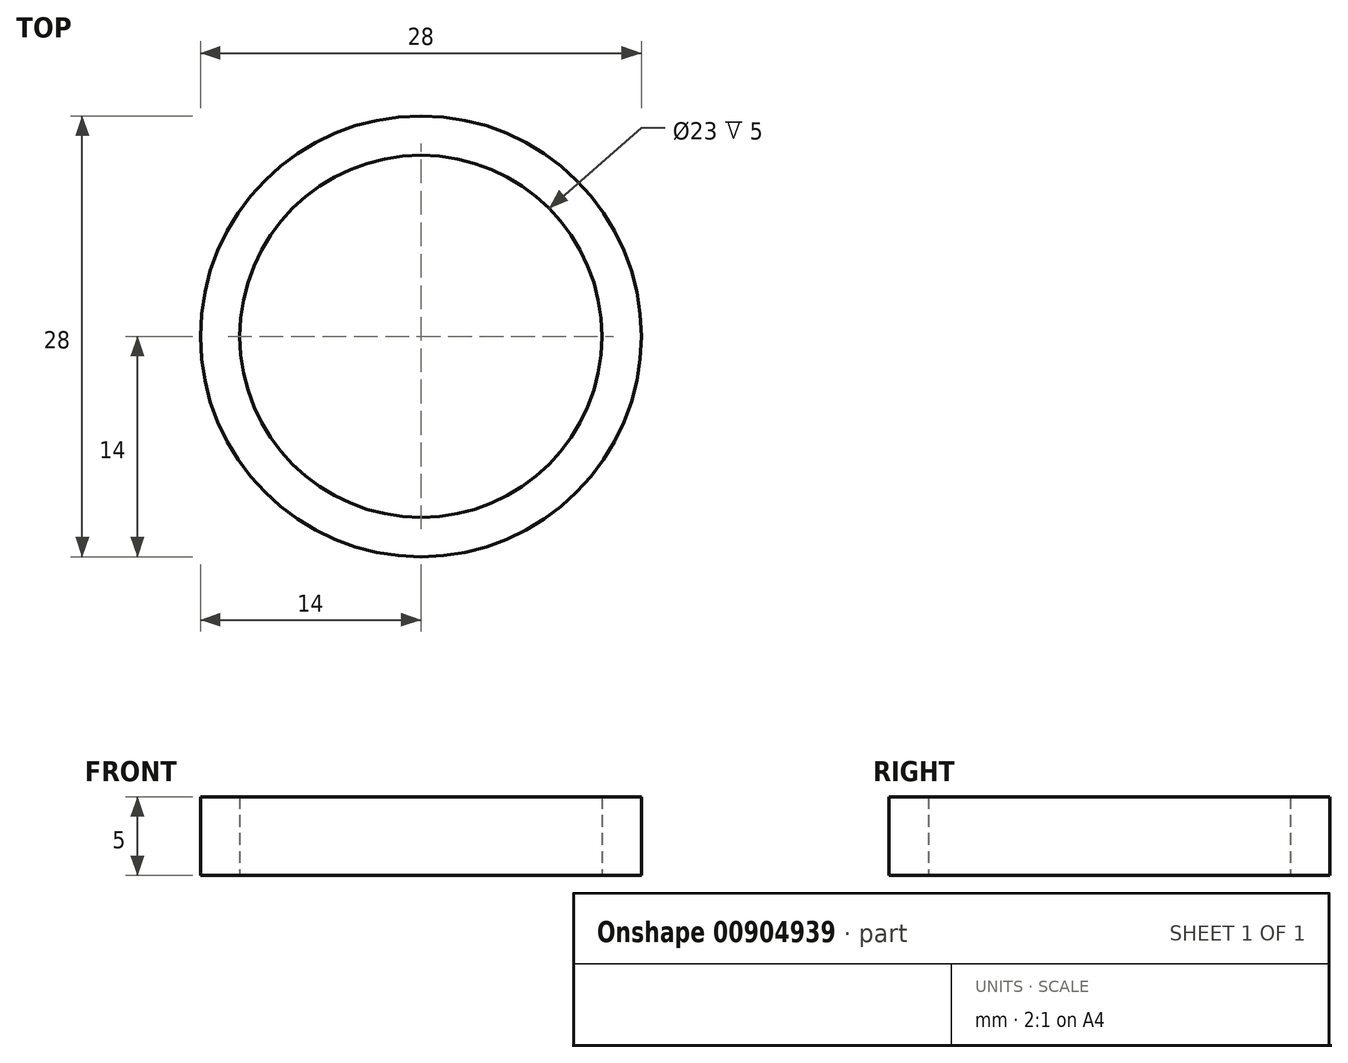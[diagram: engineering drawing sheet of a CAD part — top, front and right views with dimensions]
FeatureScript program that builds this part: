
annotation { "Feature Type Name" : "Feature", "Feature Type Description" : "" }
export const myFeature = defineFeature(function(context is Context, id is Id, definition is map)
    precondition{}
    {
        {
            var Q0;
            Q0=qCreatedBy(makeId("Top.planeOp"),FACE);
            var sketch = newSketch(context, id + "F0", { "sketchPlane" : qUnion([Q0])});
            skCircle(sketch, "E0", {"center": v(0, 0) * mm, "radius": 11.5 * mm});
            skCircle(sketch, "E1", {"center": v(0, 0) * mm, "radius": 14 * mm});
            skSolve(sketch);
        }
        {
            var Q0;
            Q0 = qSketchRegion(id + "F0", true);
            extrude(context, id + "F1", {"entities" : qUnion([Q0]), "depth" : 5 * mm, "offsetDistance" : 25 * mm});
        }
    });
